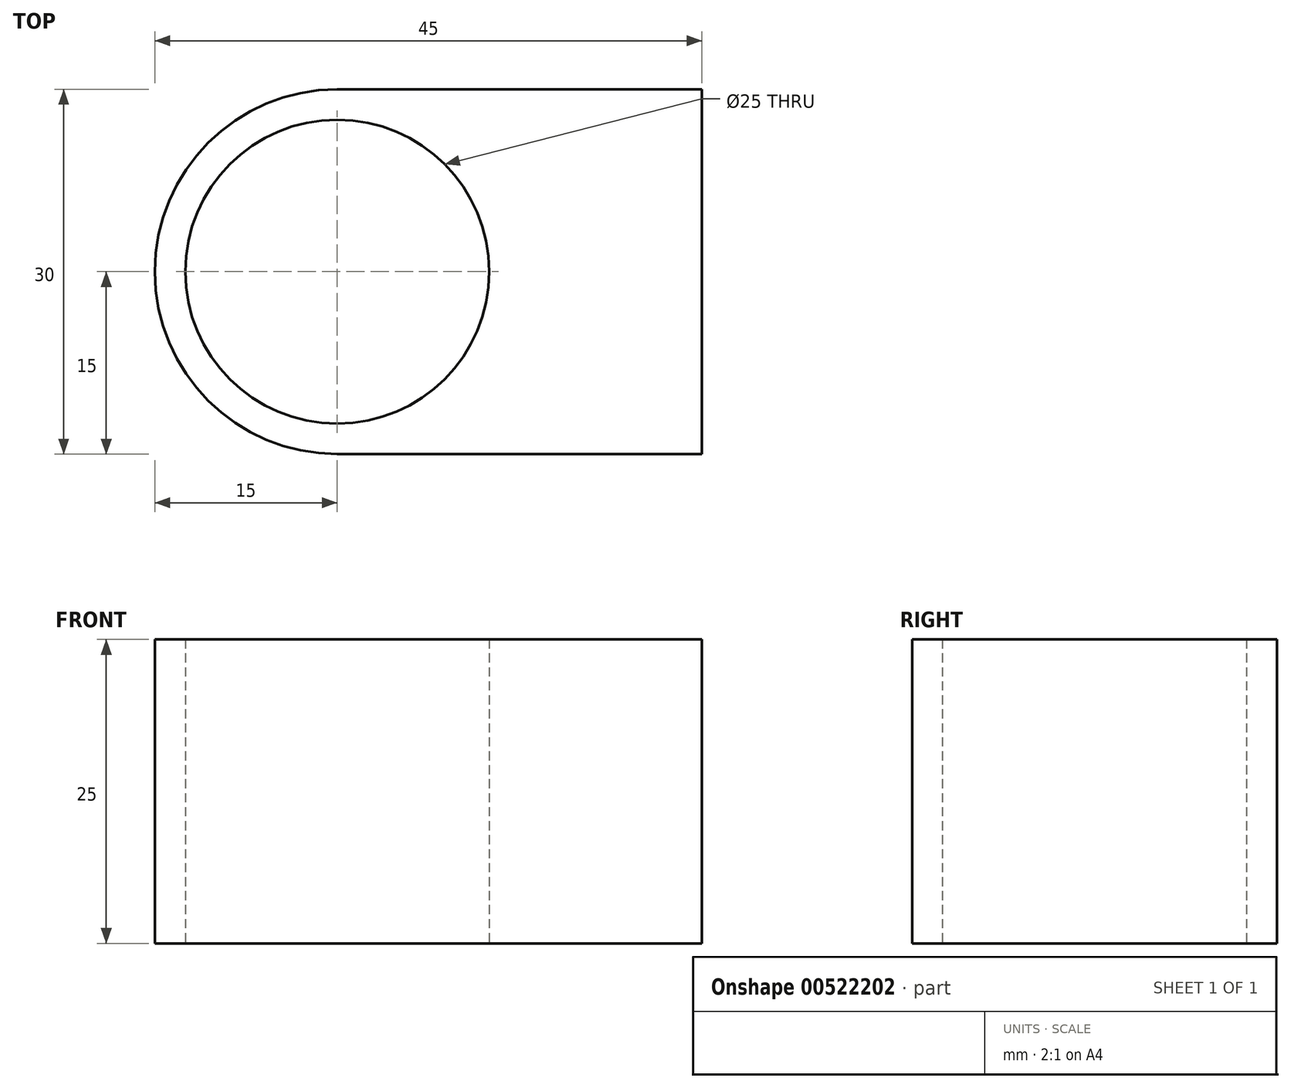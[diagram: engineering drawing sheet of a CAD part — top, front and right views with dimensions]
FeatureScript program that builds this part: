
annotation { "Feature Type Name" : "Feature", "Feature Type Description" : "" }
export const myFeature = defineFeature(function(context is Context, id is Id, definition is map)
    precondition{}
    {
        {
            var Q0;
            Q0=qCreatedBy(makeId("Top.planeOp"),FACE);
            var sketch = newSketch(context, id + "F0", { "sketchPlane" : qUnion([Q0])});
            skLineSegment(sketch, "E0.bottom", {"start": v(0, 0) * mm, "end": v(30, 0) * mm});
            skLineSegment(sketch, "E0.top", {"start": v(0, -30) * mm, "end": v(30, -30) * mm});
            skLineSegment(sketch, "E0.left", {"start": v(0, 0) * mm, "end": v(0, -30) * mm});
            skLineSegment(sketch, "E0.right", {"start": v(30, 0) * mm, "end": v(30, -30) * mm});
            skCircle(sketch, "E1", {"center": v(0, -15) * mm, "radius": 15 * mm});
            skCircle(sketch, "E2", {"center": v(0, -15) * mm, "radius": 12.5 * mm});
            skSolve(sketch);
        }
        {
            var Q0;
            Q0 = qSketchRegion(id + "F0", true);
            var Q1;
            {var subQ0=sQuery(id+"F0.wireOp",EDGE,"E0.bottom");Q1=makeQuery(id+"F0.imprint","IMPRINT",FACE,{"disambiguationData":[TD([[makeQuery(id+"F0.imprint","IMPRINT",EDGE,{"derivedFrom":subQ0}),-1.0]])]});}
            extrude(context, id + "F1", {"entities" : qUnion([Q0, Q1]), "depth" : 25 * mm, "offsetDistance" : 25 * mm});
        }
    });
